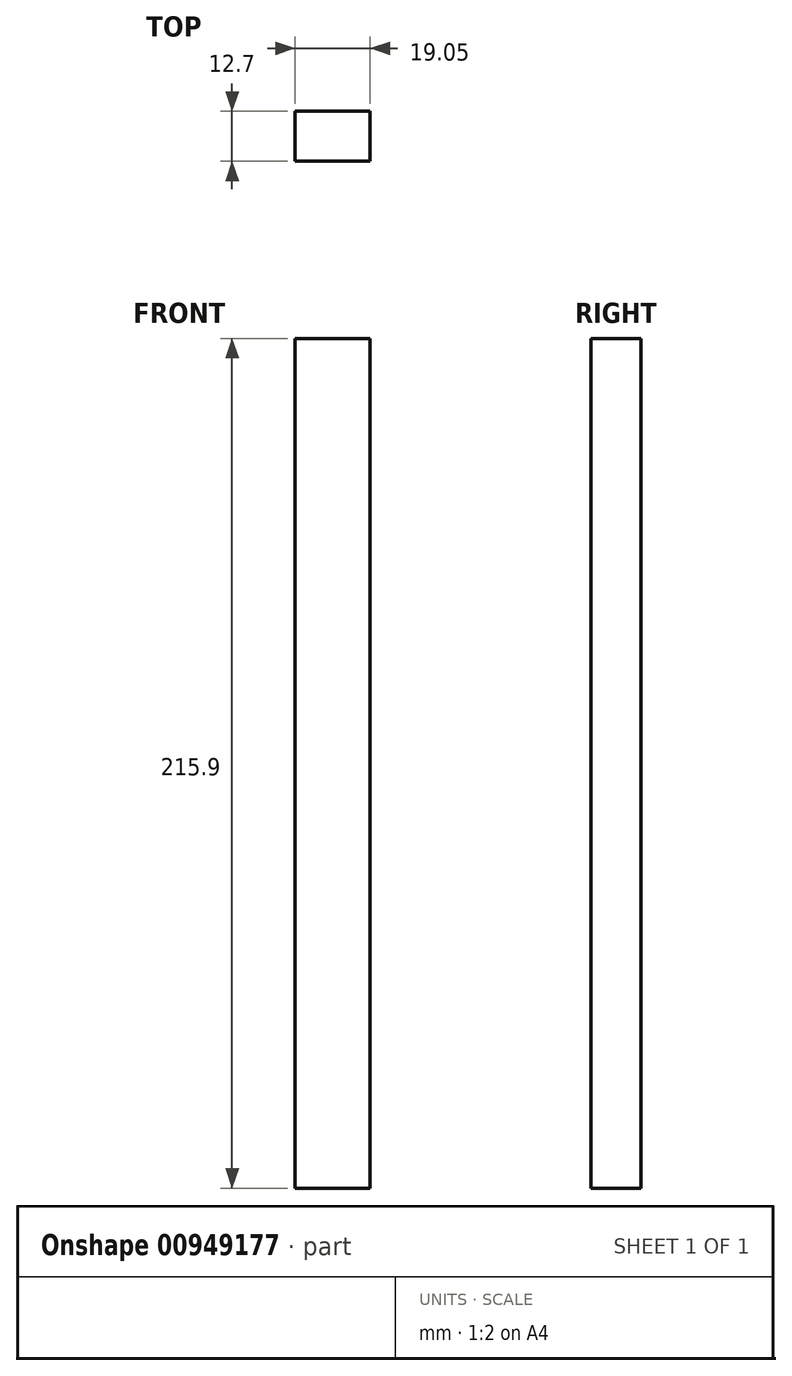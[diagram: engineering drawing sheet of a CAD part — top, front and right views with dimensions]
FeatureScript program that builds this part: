
annotation { "Feature Type Name" : "Feature", "Feature Type Description" : "" }
export const myFeature = defineFeature(function(context is Context, id is Id, definition is map)
    precondition{}
    {
        {
            var Q0;
            Q0=qCreatedBy(makeId("Front.planeOp"),FACE);
            var sketch = newSketch(context, id + "F0", { "sketchPlane" : qUnion([Q0])});
            skLineSegment(sketch, "E0.bottom", {"start": v(-6.26, 135.77) * mm, "end": v(12.8, 135.77) * mm});
            skLineSegment(sketch, "E0.top", {"start": v(-6.26, -80.13) * mm, "end": v(12.8, -80.13) * mm});
            skLineSegment(sketch, "E0.left", {"start": v(-6.26, 135.77) * mm, "end": v(-6.26, -80.13) * mm});
            skLineSegment(sketch, "E0.right", {"start": v(12.8, 135.77) * mm, "end": v(12.8, -80.13) * mm});
            skSolve(sketch);
        }
        {
            var Q0;
            Q0=makeQuery(id+"F0.imprint","IMPRINT",FACE,{"disambiguationData":[TD([[makeQuery(id+"F0.imprint","IMPRINT",EDGE,{"derivedFrom":sQuery(id+"F0.wireOp",EDGE,"E0.bottom")}),-1.0]])]});
            extrude(context, id + "F1", {"entities" : qUnion([Q0]), "depth" : 12.7 * mm, "offsetDistance" : 25.4 * mm});
        }
    });
